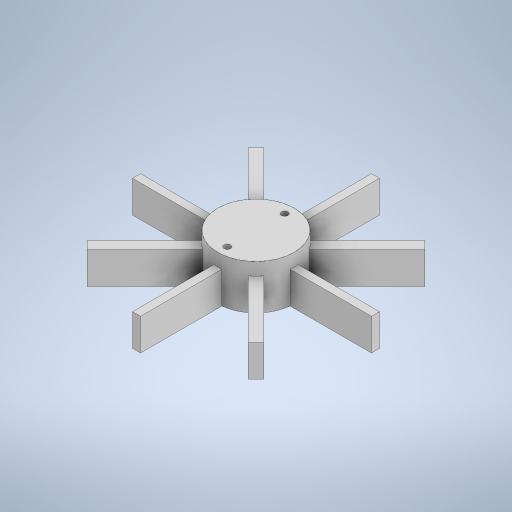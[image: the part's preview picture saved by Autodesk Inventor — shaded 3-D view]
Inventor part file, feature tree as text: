
AUTODESK INVENTOR PART (.ipt)
format: ipt  version: 2024 (Build 280153000, 153)  size: 303,616 bytes
history: native  units: in
note: dims shown in document units (in); Inventor stores cm internally (conversion verified against a paired STEP export)
features: extrude x3, sketch x3
ambient origin geometry x8: Origin, YZ Plane, XZ Plane, XY Plane, X Axis, Y Axis, Z Axis, Center Point
bodies: Solid1 (feature_tree)
feature tree (6):
  extrude  "Extrusion1"  Depth=2.9528in
  extrude  "Extrusion2"  Depth=2.9528in
  extrude  "Extrusion3"  Depth=0.4724in
  sketch  "Sketch2"  dims[d0=0.9449in d1=2.9528in]
  sketch  "Sketch3"  dims[d2=0.0984in d3=2.9528in]
  sketch  "Sketch4"  dims[d4=0.0984in d5=1.4764in d6=1.4764in d7=1.4764in d8=1.4764in d9=0.3937in d10=0.0in d11=0.9449in d12=0.1575in d13=0.0in d14=0.4724in d15=90.0deg d16=0.9449in d17=0.0in d18=0.1181in d19=90.0deg d20=0.1181in d21=90.0deg d22=0.0787in d23=0.0787in d24=0.7874in d25=0.0in]
